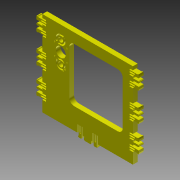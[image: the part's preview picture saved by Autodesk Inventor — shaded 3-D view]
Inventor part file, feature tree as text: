
AUTODESK INVENTOR PART (.ipt)
format: ipt  version: 2012 SP1 (Build 160190100, 190)  size: 686,080 bytes
history: native  units: in
note: dims shown in document units (in); Inventor stores cm internally (conversion verified against a paired STEP export)
features: other x5, extrude x3
ambient origin geometry x8: Origin, YZ Plane, XZ Plane, XY Plane, X Axis, Y Axis, Z Axis, Center Point
bodies: Solid1 (feature_tree)
feature tree (8):
  other  "skeleton.ipt"
  other  "DRILL-THROUGH"
  other  "POCKET_1-8"
  other  "STOCK_12MM"
  extrude  "Extrusion1"  Depth=0.3937in
  extrude  "Extrusion2"  Depth=0.4724in
  extrude  "Extrusion3"  TaperAngle=0.0deg  [1 undecoded]
  other  "THROUGH-CUT"
note: 1 required parameter value undecoded (feature->parameter linkage not recoverable at this tier; creation-order binding heuristic only, values carry confidence <= 0.55)
